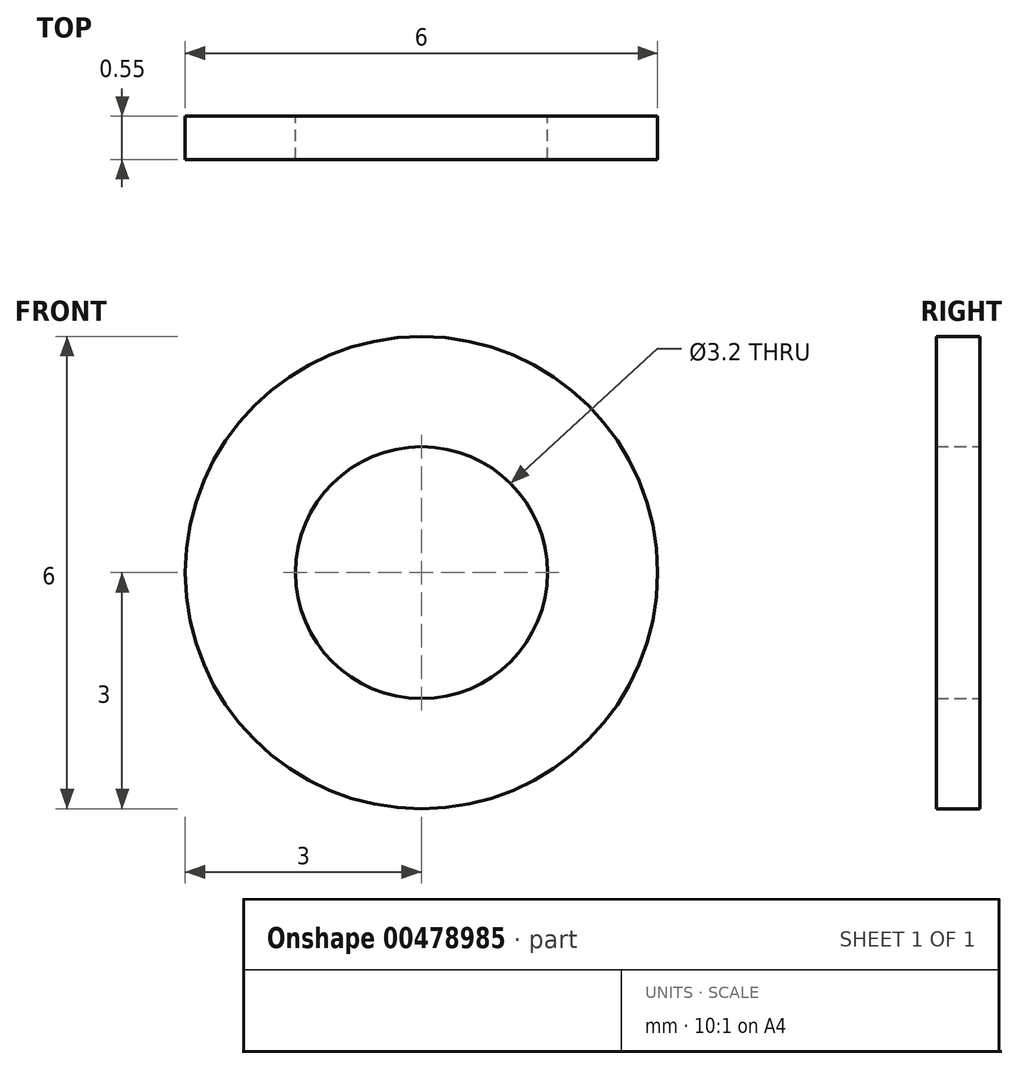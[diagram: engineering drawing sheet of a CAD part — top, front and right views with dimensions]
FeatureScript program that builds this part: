
annotation { "Feature Type Name" : "Feature", "Feature Type Description" : "" }
export const myFeature = defineFeature(function(context is Context, id is Id, definition is map)
    precondition{}
    {
        {
            var Q0;
            Q0=qCreatedBy(makeId("Front.planeOp"),FACE);
            var sketch = newSketch(context, id + "F0", { "sketchPlane" : qUnion([Q0])});
            skCircle(sketch, "E0", {"center": v(0, 0) * mm, "radius": 3 * mm});
            skCircle(sketch, "E1", {"center": v(0, 0) * mm, "radius": 1.6 * mm});
            skSolve(sketch);
        }
        {
            var Q0;
            Q0 = qSketchRegion(id + "F0", true);
            extrude(context, id + "F1", {"entities" : qUnion([Q0]), "depth" : 0.55 * mm});
        }
    });
